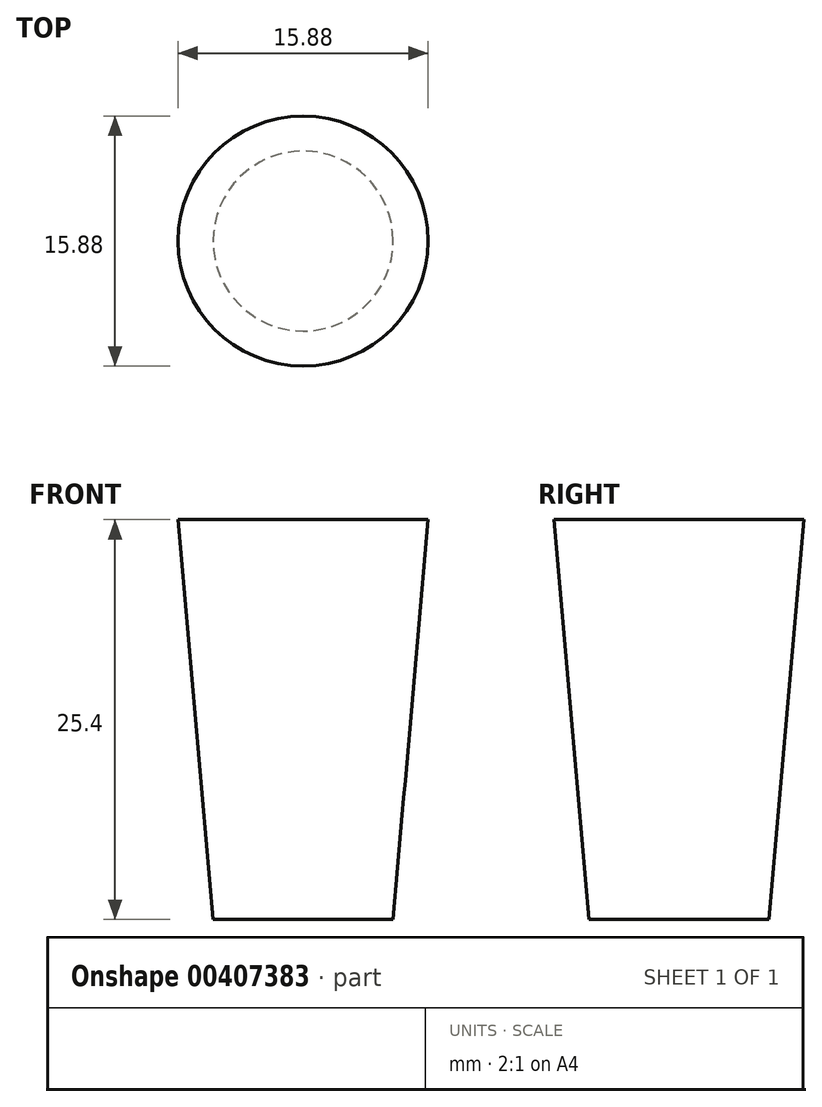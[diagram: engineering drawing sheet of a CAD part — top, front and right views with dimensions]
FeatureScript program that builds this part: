
annotation { "Feature Type Name" : "Feature", "Feature Type Description" : "" }
export const myFeature = defineFeature(function(context is Context, id is Id, definition is map)
    precondition{}
    {
        {
            var Q0;
            Q0=qCreatedBy(makeId("Top.planeOp"),FACE);
            var sketch = newSketch(context, id + "F0", { "sketchPlane" : qUnion([Q0])});
            skCircle(sketch, "E0", {"center": v(0, 0) * mm, "radius": 5.72 * mm});
            skLineSegment(sketch, "E1", {"start": v(0, 0) * mm, "end": v(0, 29.78) * mm, "construction": true});
            skSolve(sketch);
        }
        {
            var Q0;
            Q0 = qSketchRegion(id + "F0", true);
            extrude(context, id + "F1", {"entities" : qUnion([Q0]), "depth" : 25.4 * mm, "hasDraft" : true, "draftAngle" : 5 * degree, "offsetDistance" : 25.4 * mm});
        }
    });
